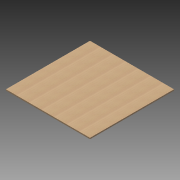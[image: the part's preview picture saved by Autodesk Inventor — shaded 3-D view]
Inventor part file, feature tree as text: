
AUTODESK INVENTOR PART (.ipt)
format: ipt  version: 2013 SP1 (Build 170176100, 176)  size: 93,184 bytes
history: native  units: mm
features: extrude x1, sketch x1
ambient origin geometry x8: Origin, YZ Plane, XZ Plane, XY Plane, X Axis, Y Axis, Z Axis, Center Point
bodies: Volumenkörper1 (feature_tree)
feature tree (2):
  extrude  "Extrusion1"  Depth=402.0mm
  sketch  "Skizze1"  dims[d0=402.0mm d1=402.0mm d2=6.0mm d3=0.0mm]
